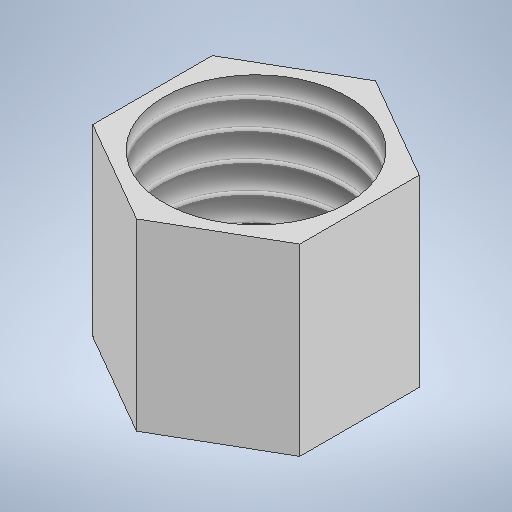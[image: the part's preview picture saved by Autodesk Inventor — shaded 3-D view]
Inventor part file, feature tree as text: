
AUTODESK INVENTOR PART (.ipt)
format: ipt  version: 2025.1 (Build 291241000, 241)  size: 271,872 bytes
history: native  units: mm
features: sketch x3, hole x2, extrude x1, thread x1
ambient origin geometry x8: Origin, YZ Plane, XZ Plane, XY Plane, X Axis, Y Axis, Z Axis, Center Point
bodies: Solid1 (feature_tree)
feature tree (7):
  extrude  "Extrusion1"  Depth=10.0mm TaperAngle=0.0deg
  hole  "Hole1"  [1 undecoded]
  thread  "Thread1"  [1 undecoded]
  hole  "Hole2"  [1 undecoded]
  sketch  "Sketch1"  dims[d0=13.0mm d1=10.0mm d2=0.0mm]
  sketch  "Sketch2"  dims[d3=10.0mm d4=6.0mm d5=4.0mm d6=2.0mm d7=90.0deg d8=7.0mm d9=0.0mm d10=10.0mm d11=0.0mm]
  sketch  "Sketch3"  dims[d12=6.0mm d13=6.0mm d14=4.0mm d15=2.0mm d16=90.0deg d17=4.0mm d18=0.0mm]
note: 3 required parameter values undecoded (feature->parameter linkage not recoverable at this tier; creation-order binding heuristic only, values carry confidence <= 0.55)
